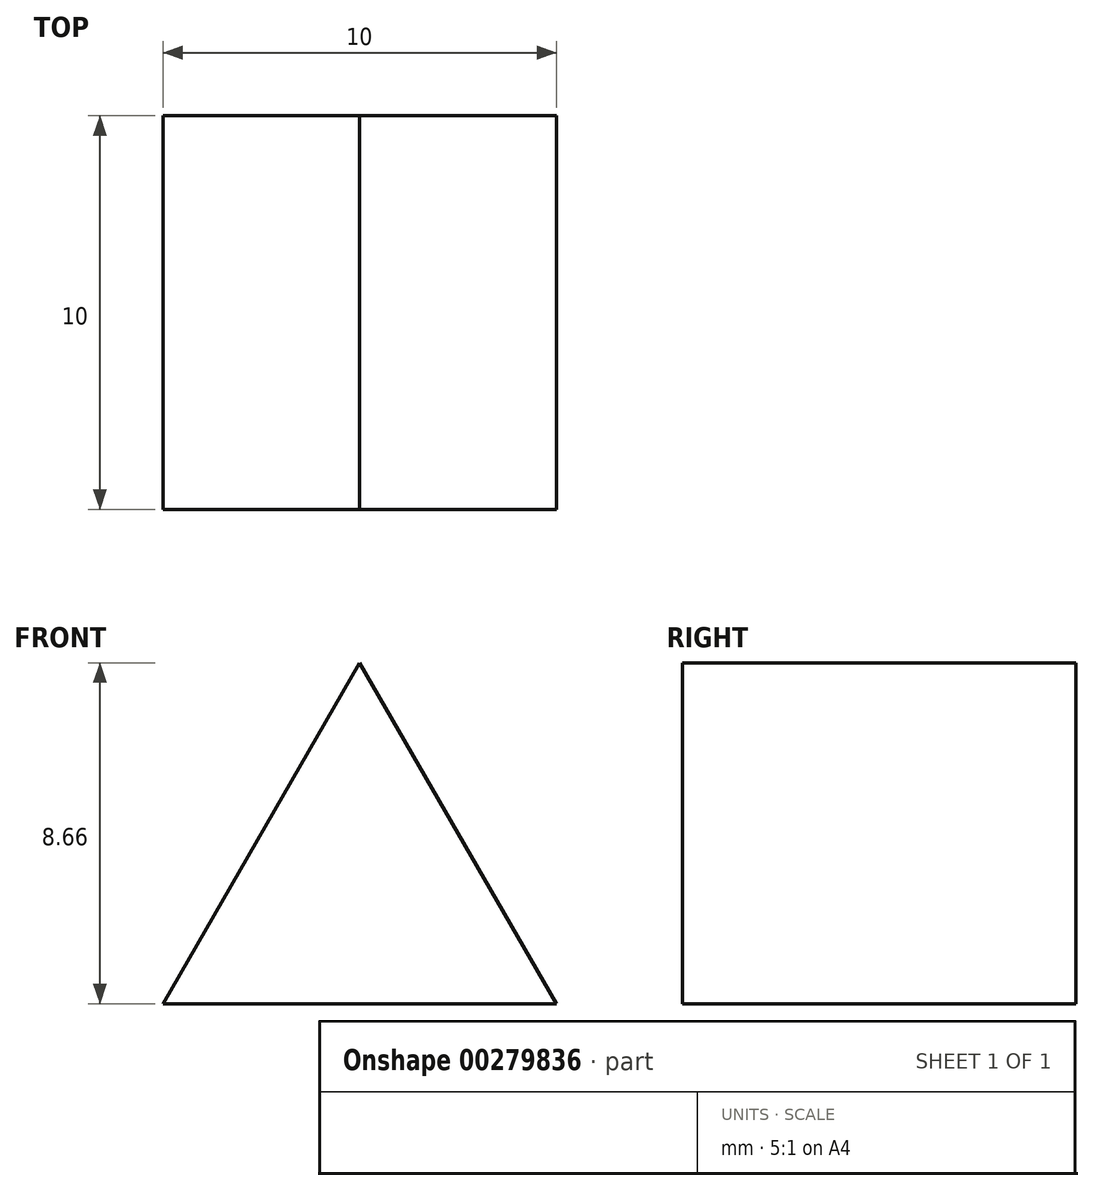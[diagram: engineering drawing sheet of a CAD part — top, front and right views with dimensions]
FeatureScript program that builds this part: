
annotation { "Feature Type Name" : "Feature", "Feature Type Description" : "" }
export const myFeature = defineFeature(function(context is Context, id is Id, definition is map)
    precondition{}
    {
        {
            var Q0;
            Q0=qCreatedBy(makeId("Front.planeOp"),FACE);
            var sketch = newSketch(context, id + "F0", { "sketchPlane" : qUnion([Q0])});
            skLineSegment(sketch, "E0", {"start": v(0, 0) * mm, "end": v(5, 8.66) * mm});
            skLineSegment(sketch, "E1", {"start": v(5, 8.66) * mm, "end": v(10, 0) * mm});
            skLineSegment(sketch, "E2", {"start": v(10, 0) * mm, "end": v(0, 0) * mm});
            skSolve(sketch);
        }
        {
            var Q0;
            Q0 = qSketchRegion(id + "F0", true);
            extrude(context, id + "F1", {"entities" : qUnion([Q0]), "depth" : 10 * mm});
        }
    });
